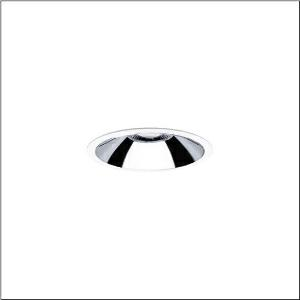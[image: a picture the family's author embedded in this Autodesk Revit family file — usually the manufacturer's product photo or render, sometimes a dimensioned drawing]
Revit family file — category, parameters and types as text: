
# Revit family: lunis_21_l_51db15md4c
name_source: partatom
category: Lighting Fixtures
units: mm (PartAtom-declared; Revit-internal decimal feet)

## family parameters
Cut with Voids When Loaded = No
Host = Face
Light Source = No
Part Type = Normal
Room Calculation Point = No
Round Connector Dimension = Use Diameter
Shared = No

## types (1)
- --- (1 x LED, 1700 lm, 13.8 W, 4000K)
    Apparent Load = 14 VA
    CIE Flux Codes = 90 99 100 100 100
    Color Rendering = 80
    Color Temperature = 4000K
    Default Elevation = 1800 mm
    Description = Lunis 21,  L, downlight, of PC, light emission: direct distribution, LED rated luminous flux: 1.700lm, light colour: 840, control gear: ECG, with terminal, 3-pole, mains connection: 220..240V, AC, housing, round, of diecast aluminium, traffic white (RAL 9016), diameter: 162mm, protection rating (complete): IP20, protection rating (on room side): IP54, insulation class (complete): insulation class II (safety insulation), certification: CE, impact resistance: IK02, packaging unit: 1 piece
    Height = 0 mm  [stored 0 ft]
    Lamp = 1 x LED
    Lamp Light Flux = 1700 lm
    Lamp Power = 13.8 W
    Lamp count = 1
    Length = 162 mm
    Luminous efficacy = 123 lm/W
    Manufacturer = Siteco
    ModVariant = No
    Model = 51DB15MD4C
    Mounting Place = Ceiling
    Mounting Type = Recessed
    Number of Poles = 1
    OnlyDefault = Yes
    Power Factor = 1
    Product Name = Lunis 21 L
    Product group = downlight
    ProductGroupID = 400
    Protection Class = Protection class II
    Protection Degree = IP 20
    RLX_Detail_Level = 1
    RLX_Emergency_Light_Flux = 0 lm
    RLX_Emergency_Type = 0
    RLX_Emergency_Type_DB = No
    RlxData = <blob elided: 21877 chars, md5=6f73aaae>
    Socket = socket
    Standby Power = 0 W
    System Light Flux = 1700 lm
    System Power = 14 W
    Type Comments = factory setting: luminous flux: 100 % | (ON | ON)
    Type Image = l_1287387.jpg
    URL = http://relux.com
    VarID = @adj_117421
    Voltage = 0 V
    Weight = 0.00 kg
    Width = 0 mm  [stored 0 ft]

note: [stored X ft] marks values corroborated as IEEE doubles in the binary element streams (Revit-internal decimal feet)

## geometry (parser evidence)
native form markers: Blend x4, Sweep x11
no freeform markers — native parametric forms only
